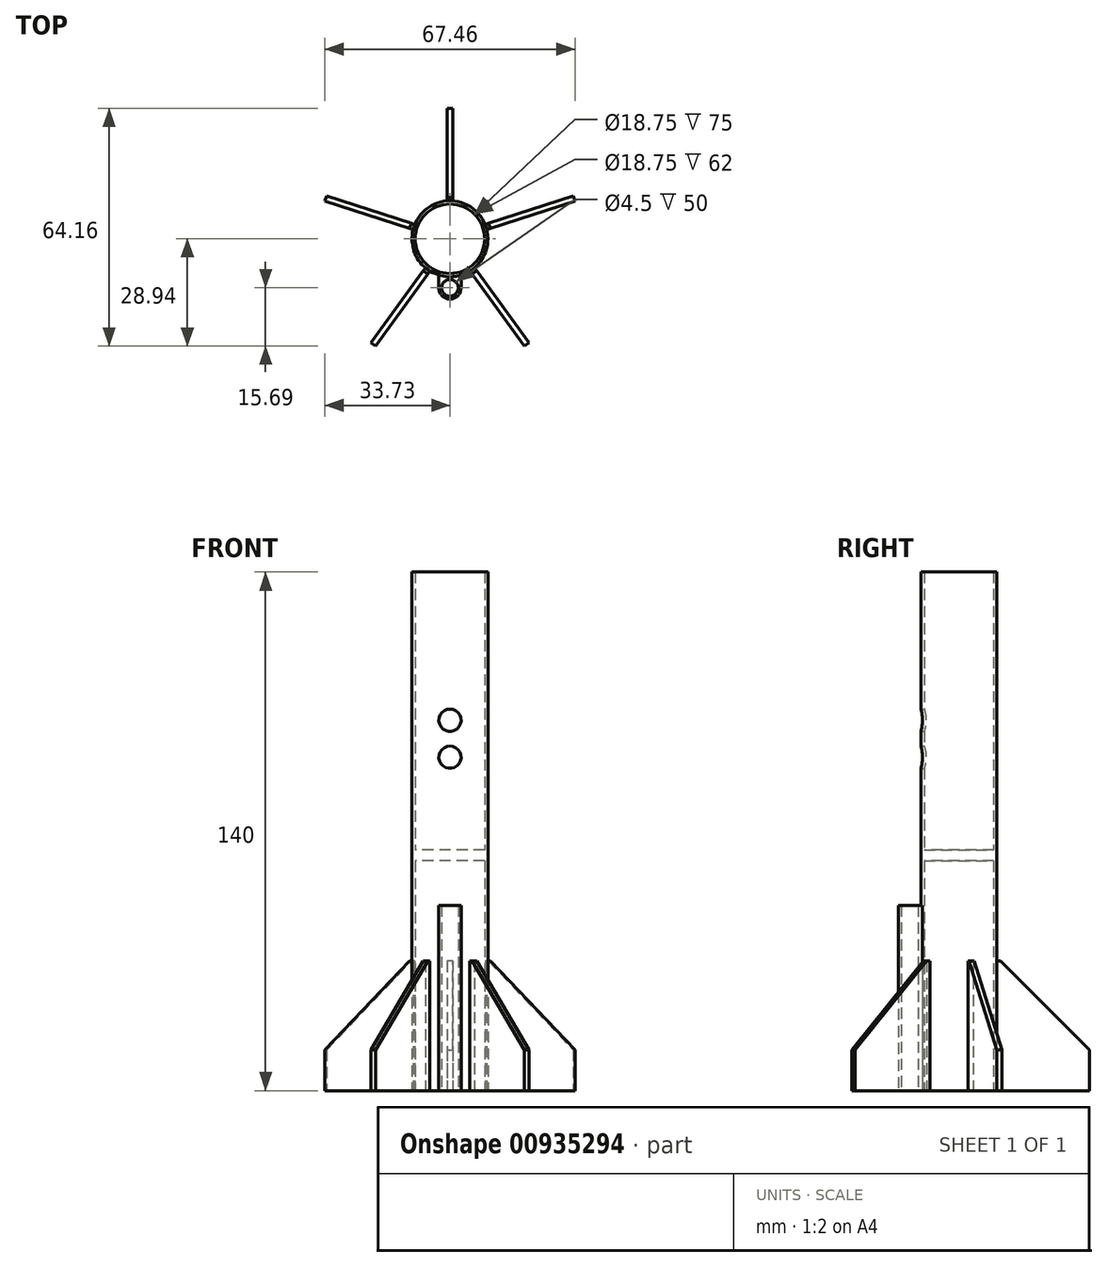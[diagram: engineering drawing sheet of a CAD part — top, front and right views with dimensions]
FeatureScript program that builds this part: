
annotation { "Feature Type Name" : "Feature", "Feature Type Description" : "" }
export const myFeature = defineFeature(function(context is Context, id is Id, definition is map)
    precondition{}
    {
        {
            var Q0;
            Q0=qCreatedBy(makeId("Top.planeOp"),FACE);
            var sketch = newSketch(context, id + "F0", { "sketchPlane" : qUnion([Q0])});
            skCircle(sketch, "E0", {"center": v(0, 0) * mm, "radius": 9.38 * mm});
            skCircle(sketch, "E1", {"center": v(0, 0) * mm, "radius": 10.25 * mm});
            skCircle(sketch, "E2", {"center": v(0, -13.25) * mm, "radius": 2.25 * mm});
            skCircle(sketch, "E3", {"center": v(0, -13.25) * mm, "radius": 3 * mm});
            skLineSegment(sketch, "E4", {"start": v(-3, -13.25) * mm, "end": v(-3, -9.8) * mm});
            skLineSegment(sketch, "E5", {"start": v(3, -13.25) * mm, "end": v(3, -9.8) * mm});
            skLineSegment(sketch, "E6.bottom", {"start": v(0.75, 35.22) * mm, "end": v(-0.75, 35.22) * mm});
            skLineSegment(sketch, "E6.top", {"start": v(0.75, 10.22) * mm, "end": v(-0.75, 10.22) * mm, "construction": true});
            skLineSegment(sketch, "E6.left", {"start": v(0.75, 35.22) * mm, "end": v(0.75, 10.22) * mm});
            skLineSegment(sketch, "E6.right", {"start": v(-0.75, 35.22) * mm, "end": v(-0.75, 10.22) * mm});
            skCircle(sketch, "E7", {"center": v(0, 0) * mm, "radius": 7.5 * mm});
            skSolve(sketch);
        }
        {
            var Q0;
            Q0=makeQuery(id+"F0.imprint","IMPRINT",FACE,{"disambiguationData":[TD([[makeQuery(id+"F0.imprint","IMPRINT",EDGE,{"derivedFrom":sQuery(id+"F0.wireOp",EDGE,"E0")}),-1.0]])]});
            extrude(context, id + "F1", {"entities" : qUnion([Q0]), "depth" : 140 * mm, "offsetDistance" : 25 * mm});
        }
        {
            var Q0;
            Q0=makeQuery(id+"F0.imprint","IMPRINT",FACE,{"disambiguationData":[TD([[makeQuery(id+"F0.imprint","IMPRINT",EDGE,{"derivedFrom":sQuery(id+"F0.wireOp",EDGE,"E6.bottom")}),1.0]])]});
            extrude(context, id + "F2", {"entities" : qUnion([Q0]), "operationType" : NewBodyOperationType.ADD, "depth" : 35 * mm, "offsetDistance" : 25 * mm});
        }
        {
            var Q0;
            Q0=makeQuery(id+"F2.opExtrude","CAP_EDGE",EDGE,{"disambiguationData":[OSD([sQuery(id+"F0.wireOp",EDGE,"E6.bottom")])],"isStart":false});
            chamfer(context, id + "F3", {"entities" : qUnion([Q0]), "width" : 24 * mm, "tangentPropagation" : true});
        }
        {
            var Q0;
            Q0=makeQuery(id+"F1.opExtrude","SWEPT_BODY",BODY,{"disambiguationData":[OSD([sQuery(id+"F0.wireOp",EDGE,"E0"),sQuery(id+"F0.wireOp",EDGE,"E1")])]});
            var Q1;
            Q1=makeQuery(id+"F1.opExtrude","CAP_EDGE",EDGE,{"disambiguationData":[OSD([sQuery(id+"F0.wireOp",EDGE,"E0")])],"isStart":false});
            circularPattern(context, id + "F4", {"operationType" : NewBodyOperationType.ADD, "entities" : qUnion([Q0]), "axis" : qUnion([Q1]), "angle" : 360 * degree, "instanceCount" : 5, "equalSpace" : true});
        }
        {
            var Q0;
            Q0=makeQuery(id+"F0.imprint","IMPRINT",FACE,{"disambiguationData":[TD([[makeQuery(id+"F0.imprint","IMPRINT",EDGE,{"derivedFrom":sQuery(id+"F0.wireOp",EDGE,"E2")}),-1.0]])]});
            var Q1;
            {var subQ0=sQuery(id+"F0.wireOp",EDGE,"E5");Q1=makeQuery(id+"F0.imprint","IMPRINT",FACE,{"disambiguationData":[TD([[makeQuery(id+"F0.imprint","IMPRINT",EDGE,{"derivedFrom":subQ0}),1.0]])]});}
            var Q2;
            {var subQ0=sQuery(id+"F0.wireOp",EDGE,"E4");Q2=makeQuery(id+"F0.imprint","IMPRINT",FACE,{"disambiguationData":[TD([[makeQuery(id+"F0.imprint","IMPRINT",EDGE,{"derivedFrom":subQ0}),-1.0]])]});}
            extrude(context, id + "F5", {"entities" : qUnion([Q0, Q1, Q2]), "operationType" : NewBodyOperationType.ADD, "depth" : 50 * mm, "offsetDistance" : 25 * mm});
        }
        {
            var Q0;
            Q0=makeQuery(id+"F0.imprint","IMPRINT",FACE,{"disambiguationData":[TD([[makeQuery(id+"F0.imprint","IMPRINT",EDGE,{"derivedFrom":sQuery(id+"F0.wireOp",EDGE,"E7")}),1.0]])]});
            var Q1;
            Q1=makeQuery(id+"F0.imprint","IMPRINT",FACE,{"disambiguationData":[TD([[makeQuery(id+"F0.imprint","IMPRINT",EDGE,{"derivedFrom":sQuery(id+"F0.wireOp",EDGE,"E0")}),1.0]])]});
            var Q2;
            Q2=sQuery(id+"F0.wireOp",EDGE,"E7");
            var Q3;
            Q3=sQuery(id+"F0.wireOp",EDGE,"E0");
            extrude(context, id + "F6", {"entities" : qUnion([Q0, Q1]), "operationType" : NewBodyOperationType.ADD, "surfaceEntities" : qUnion([Q2, Q3]), "depth" : 65 * mm, "offsetDistance" : 25 * mm, "hasSecondDirection" : true, "secondDirectionOppositeDirection" : false, "secondDirectionDepth" : 62 * mm});
        }
        {
            var Q0;
            Q0=qCreatedBy(makeId("Front.planeOp"),FACE);
            var sketch = newSketch(context, id + "F7", { "sketchPlane" : qUnion([Q0])});
            skCircle(sketch, "E8", {"center": v(0, 100) * mm, "radius": 3 * mm});
            skCircle(sketch, "E9", {"center": v(0, 90) * mm, "radius": 3 * mm});
            skSolve(sketch);
        }
        {
            var Q0;
            Q0 = qSketchRegion(id + "F7", true);
            extrude(context, id + "F8", {"entities" : qUnion([Q0]), "operationType" : NewBodyOperationType.REMOVE, "endBound" : BoundingType.THROUGH_ALL, "depth" : 25 * mm, "offsetDistance" : 25 * mm});
        }
    });
